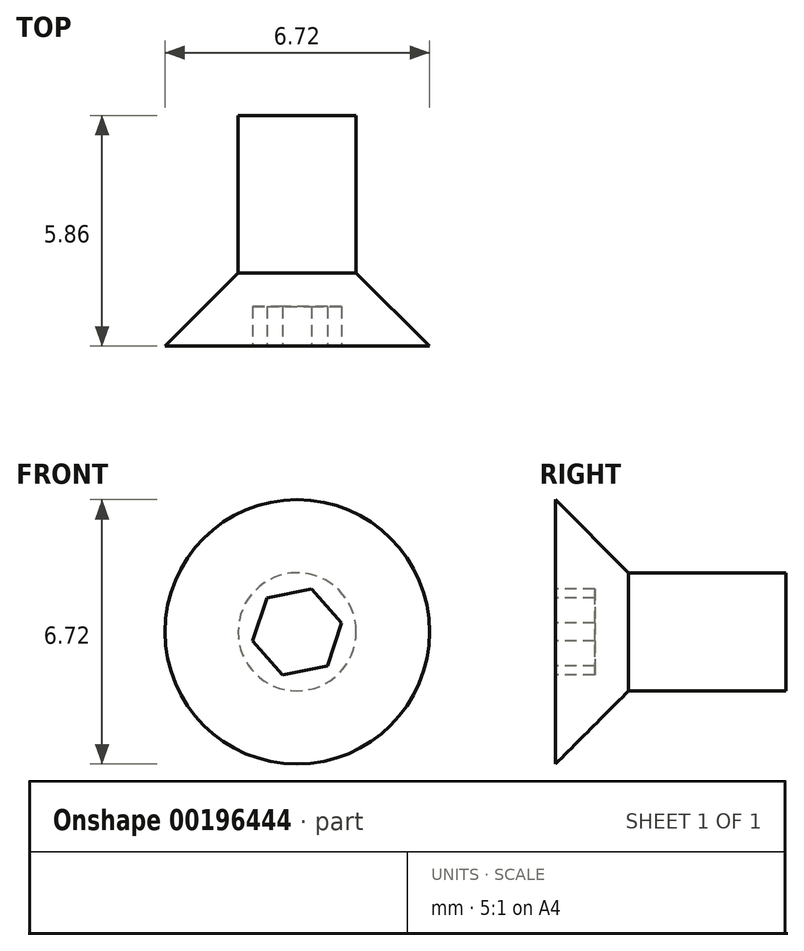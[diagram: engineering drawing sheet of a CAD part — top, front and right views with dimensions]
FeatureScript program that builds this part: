
annotation { "Feature Type Name" : "Feature", "Feature Type Description" : "" }
export const myFeature = defineFeature(function(context is Context, id is Id, definition is map)
    precondition{}
    {
        {
            var Q0;
            Q0=qCreatedBy(makeId("Front.planeOp"),FACE);
            var sketch = newSketch(context, id + "F0", { "sketchPlane" : qUnion([Q0])});
            skCircle(sketch, "E0", {"center": v(0, 0) * mm, "radius": 1.5 * mm});
            skSolve(sketch);
        }
        {
            var Q0;
            Q0=qCreatedBy(makeId("Front.planeOp"),FACE);
            cPlane(context, id + "F1", {"entities" : qUnion([Q0]), "cplaneType" : CPlaneType.OFFSET, "offset" : 1.86 * mm, "width" : 150 * mm, "height" : 150 * mm});
        }
        {
            var Q0;
            Q0=qCreatedBy(id+"F1.planeOp",FACE);
            var sketch = newSketch(context, id + "F2", { "sketchPlane" : qUnion([Q0])});
            skCircle(sketch, "E1", {"center": v(0, 0) * mm, "radius": 3.36 * mm});
            skSolve(sketch);
        }
        {
            var Q0;
            Q0=makeQuery(id+"F0.imprint","IMPRINT",FACE,{"disambiguationData":[TD([[makeQuery(id+"F0.imprint","IMPRINT",EDGE,{"derivedFrom":sQuery(id+"F0.wireOp",EDGE,"E0")}),1.0]])]});
            var Q1;
            Q1=makeQuery(id+"F2.imprint","IMPRINT",FACE,{"disambiguationData":[TD([[makeQuery(id+"F2.imprint","IMPRINT",EDGE,{"derivedFrom":sQuery(id+"F2.wireOp",EDGE,"E1")}),1.0]])]});
            loft(context, id + "F3", {"sheetProfilesArray" : [{ "sheetProfileEntities" : qUnion([Q0]) }, { "sheetProfileEntities" : qUnion([Q1]) }]});
        }
        {
            var Q0;
            Q0=makeQuery(id+"F3.opLoft","CAP_FACE",FACE,{"disambiguationData":[OSD([makeQuery(id+"F2.imprint","IMPRINT",FACE,{"disambiguationData":[TD([[makeQuery(id+"F2.imprint","IMPRINT",EDGE,{"derivedFrom":sQuery(id+"F2.wireOp",EDGE,"E1")}),1.0]])]})])],"isStart":true});
            var sketch = newSketch(context, id + "F4", { "sketchPlane" : qUnion([Q0])});
            skCircle(sketch, "E2.cCircle", {"center": v(0, 0) * mm, "radius": 1 * mm, "construction": true});
            skLineSegment(sketch, "E2.0", {"start": v(0.37, 1.1) * mm, "end": v(1.13, 0.23) * mm});
            skLineSegment(sketch, "E2.1", {"start": v(1.13, 0.23) * mm, "end": v(0.76, -0.87) * mm});
            skLineSegment(sketch, "E2.2", {"start": v(0.76, -0.87) * mm, "end": v(-0.37, -1.1) * mm});
            skLineSegment(sketch, "E2.3", {"start": v(-0.37, -1.1) * mm, "end": v(-1.13, -0.23) * mm});
            skLineSegment(sketch, "E2.4", {"start": v(-1.13, -0.23) * mm, "end": v(-0.76, 0.87) * mm});
            skLineSegment(sketch, "E2.5", {"start": v(-0.76, 0.87) * mm, "end": v(0.37, 1.1) * mm});
            skPoint(sketch, "E2.0.midPoint", {"position": v(0.75, 0.66) * mm});
            skSolve(sketch);
        }
        {
            var Q0;
            Q0 = qSketchRegion(id + "F4", true);
            extrude(context, id + "F5", {"entities" : qUnion([Q0]), "operationType" : NewBodyOperationType.REMOVE, "oppositeDirection" : true, "depth" : 1 * mm});
        }
        {
            var Q0;
            Q0 = qSketchRegion(id + "F0", true);
            extrude(context, id + "F6", {"entities" : qUnion([Q0]), "operationType" : NewBodyOperationType.ADD, "oppositeDirection" : true, "depth" : 4 * mm});
        }
    });
